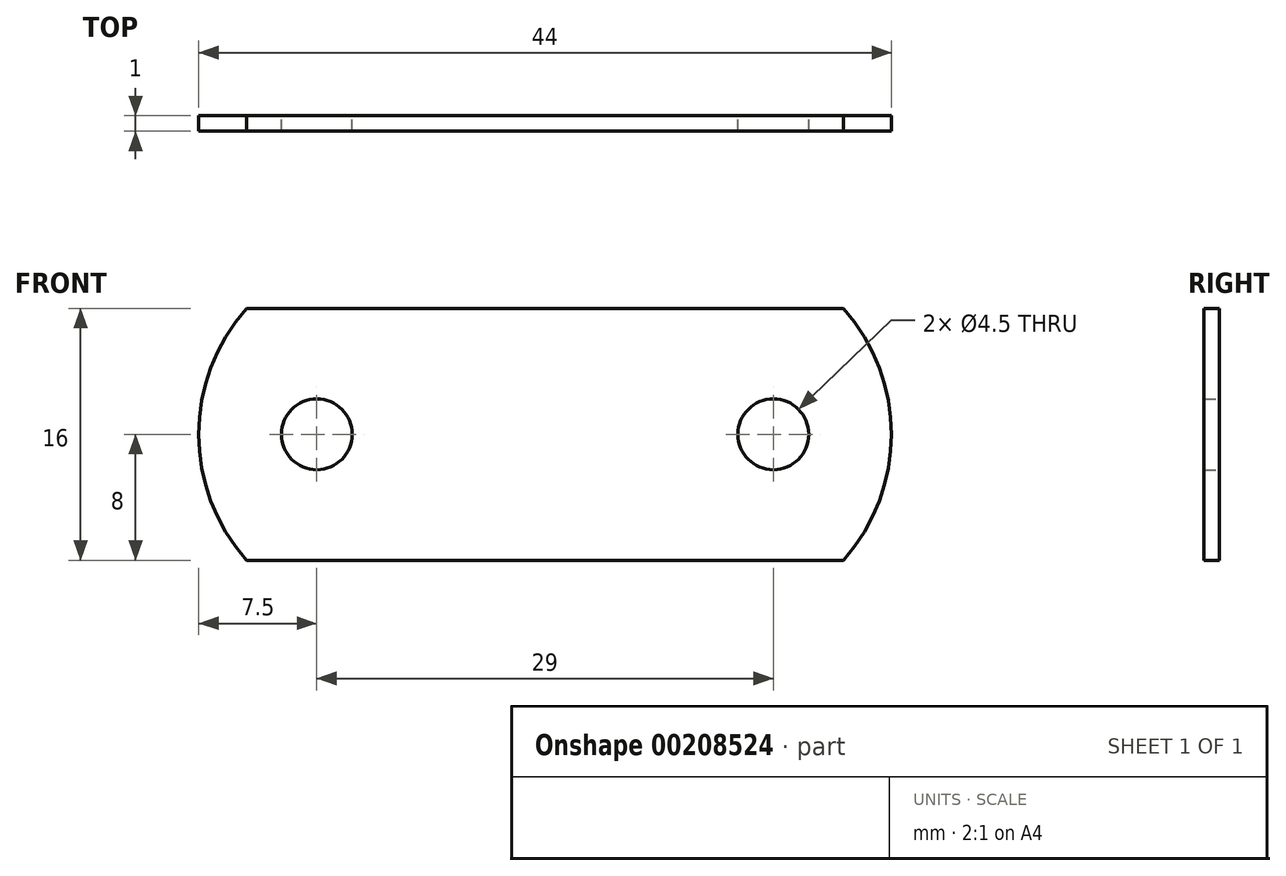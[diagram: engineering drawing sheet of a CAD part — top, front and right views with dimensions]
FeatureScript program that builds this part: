
annotation { "Feature Type Name" : "Feature", "Feature Type Description" : "" }
export const myFeature = defineFeature(function(context is Context, id is Id, definition is map)
    precondition{}
    {
        {
            var Q0;
            Q0=qCreatedBy(makeId("Front.planeOp"),FACE);
            var sketch = newSketch(context, id + "F0", { "sketchPlane" : qUnion([Q0])});
            skLineSegment(sketch, "E0", {"start": v(-36.93, 8) * mm, "end": v(57.31, 8) * mm, "construction": true});
            skLineSegment(sketch, "E1", {"start": v(-70.27, 0) * mm, "end": v(70.27, 0) * mm, "construction": true});
            skLineSegment(sketch, "E2", {"start": v(0, 54.7) * mm, "end": v(0, -60.4) * mm, "construction": true});
            skPoint(sketch, "E3", {"position": v(0, 0) * mm});
            skLineSegment(sketch, "E4", {"start": v(-22, 40.07) * mm, "end": v(-22, -39.14) * mm, "construction": true});
            skLineSegment(sketch, "E5.MirrorCS", {"start": v(22, 40.07) * mm, "end": v(22, -39.14) * mm, "construction": true});
            skLineSegment(sketch, "E6.MirrorCS", {"start": v(-36.93, -8) * mm, "end": v(57.31, -8) * mm, "construction": true});
            skArc(sketch, "E7", {"start": v(-18.94, 8) * mm, "mid": v(-22, 0) * mm, "end": v(-18.94, -8) * mm});
            skArc(sketch, "E8.MirrorCS", {"start": v(18.94, 8) * mm, "mid": v(22, 0) * mm, "end": v(18.94, -8) * mm});
            skLineSegment(sketch, "E9", {"start": v(-18.94, 8) * mm, "end": v(18.94, 8) * mm});
            skLineSegment(sketch, "E10", {"start": v(18.94, -8) * mm, "end": v(-18.94, -8) * mm});
            skCircle(sketch, "E11", {"center": v(-14.5, 0) * mm, "radius": 2.25 * mm});
            skCircle(sketch, "E12.MirrorC", {"center": v(14.5, 0) * mm, "radius": 2.25 * mm});
            skSolve(sketch);
        }
        {
            var Q0;
            Q0 = qSketchRegion(id + "F0", true);
            extrude(context, id + "F1", {"entities" : qUnion([Q0]), "depth" : 1 * mm});
        }
    });
